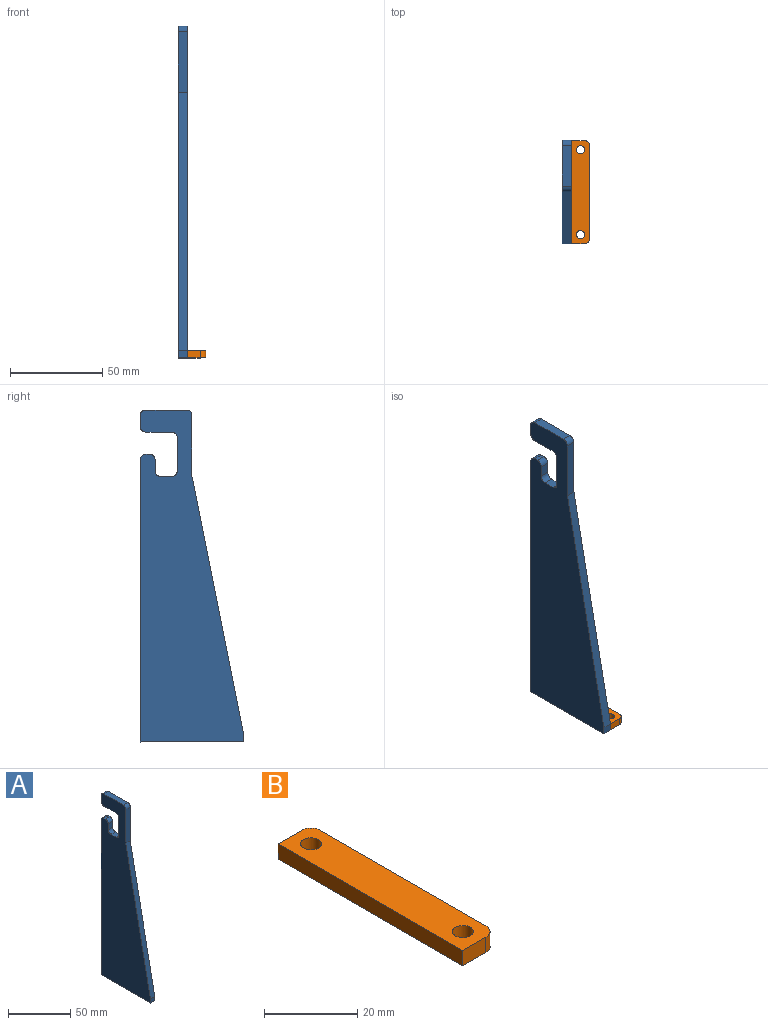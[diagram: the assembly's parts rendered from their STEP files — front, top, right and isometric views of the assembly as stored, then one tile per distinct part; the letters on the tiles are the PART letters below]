
ASSEMBLY  parts=2 mates=1
PART A: 22 faces, bbox 5x56x180 mm
  f0: plane 153x5mm, normal (0,1,0), area 765mm2, adj f3,f5,f6,f15
  f1: plane 5x4mm, normal (0,-1,0), area 20mm2, adj f3,f5,f6,f7
  f2: plane 22.01x5mm, normal (0,0,1), area 110.1mm2, adj f3,f5,f20,f21
  f3: plane 180x56.03mm, normal (1,0,0), area 6727.6mm2, adj f0,f1,f2,f4,f6,f7,f8,f9
  f4: plane 6x5mm, normal (0,1,0), area 30mm2, adj f3,f5,f16,f21
  f5: plane 180x56.03mm, normal (-1,0,0), area 6727.6mm2, adj f0,f1,f2,f4,f6,f7,f8,f9
  f6: plane 56.03x5mm, normal (0,0,-1), area 280.1mm2, adj f0,f1,f3,f5
  f7: plane 140x28.01mm, normal (0,-0.98,0.2), area 713.9mm2, adj f1,f3,f5,f8
  f8: plane 33x5mm, normal (0,-1,0), area 165mm2, adj f3,f5,f7,f20
  f9: plane 6x5mm, normal (0,-1,0), area 30mm2, adj f3,f5,f14,f19
  f10: plane 5x2mm, normal (0,0,1), area 10mm2, adj f3,f5,f14,f15
  f11: plane 14.01x5mm, normal (0,0,-1), area 70.1mm2, adj f3,f5,f16,f17
  f12: plane 18x5mm, normal (0,1,0), area 90mm2, adj f3,f5,f17,f18
  f13: plane 6.01x5mm, normal (0,0,1), area 30.1mm2, adj f3,f5,f18,f19
  f14: cylinder r=3mm len=5mm, axis (1,0,0), area 23.6mm2, adj f3,f5,f9,f10
  f15: cylinder r=3mm len=5mm, axis (-1,0,0), area 23.6mm2, adj f0,f3,f5,f10
  f16: cylinder r=3mm len=5mm, axis (-1,0,0), area 23.6mm2, adj f3,f4,f5,f11
  f17: cylinder r=3mm len=5mm, axis (-1,0,0), area 23.6mm2, adj f3,f5,f11,f12
  f18: cylinder r=3mm len=5mm, axis (-1,0,0), area 23.6mm2, adj f3,f5,f12,f13
  f19: cylinder r=3mm len=5mm, axis (-1,0,0), area 23.6mm2, adj f3,f5,f9,f13
  f20: cylinder r=3mm len=5mm, axis (-1,0,0), area 23.6mm2, adj f2,f3,f5,f8
  f21: cylinder r=3mm len=5mm, axis (1,0,0), area 23.6mm2, adj f2,f3,f4,f5
PART B: 10 faces, bbox 10x56x4 mm
  f0: plane 7x4mm, normal (0,1,0), area 28mm2, adj f1,f6,f7,f8
  f1: plane 56.03x4mm, normal (-1,0,0), area 224.1mm2, adj f0,f2,f6,f7
  f2: plane 7x4mm, normal (0,-1,0), area 28mm2, adj f1,f6,f7,f9
  f3: cylinder r=2.25mm len=4.5mm, axis (0,0,-1), area 56.5mm2, adj f6,f7
  f4: cylinder r=2.25mm len=4.5mm, axis (0,0,-1), area 56.5mm2, adj f6,f7
  f5: plane 50.03x4mm, normal (1,0,0), area 200.1mm2, adj f6,f7,f8,f9
  f6: plane 56.03x10mm, normal (0,0,1), area 524.6mm2, adj f0,f1,f2,f3,f4,f5,f8,f9
  f7: plane 56.03x10mm, normal (0,0,-1), area 524.6mm2, adj f0,f1,f2,f3,f4,f5,f8,f9
  f8: cylinder r=3mm len=4mm, axis (0,0,-1), area 18.8mm2, adj f0,f5,f6,f7
  f9: cylinder r=3mm len=4mm, axis (0,0,1), area 18.8mm2, adj f2,f5,f6,f7
PLACE A t=(-47.63,-125.09,96.71)mm
PLACE B t=(-47.63,-125.09,96.71)mm
MATE fastened B.f1 <-> A.f3  axis (-1,0,0) through (-45.13,-125.09,96.71)mm
